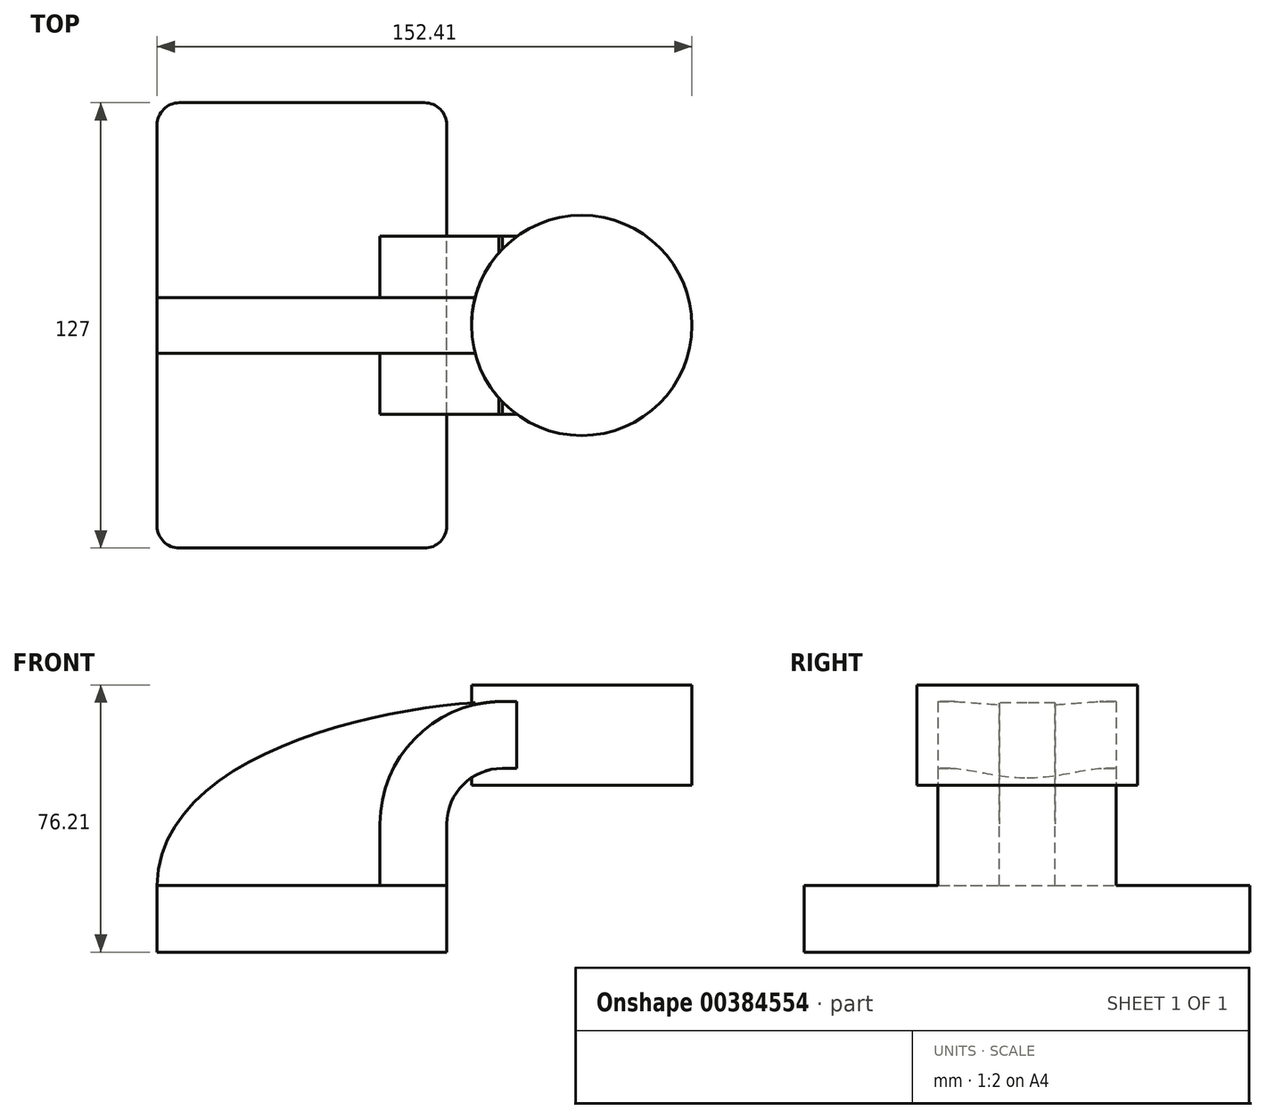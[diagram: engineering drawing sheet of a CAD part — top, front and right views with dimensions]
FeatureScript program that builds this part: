
annotation { "Feature Type Name" : "Feature", "Feature Type Description" : "" }
export const myFeature = defineFeature(function(context is Context, id is Id, definition is map)
    precondition{}
    {
        {
            var Q0;
            Q0=qCreatedBy(makeId("Front.planeOp"),FACE);
            var sketch = newSketch(context, id + "F0", { "sketchPlane" : qUnion([Q0])});
            skLineSegment(sketch, "E0.bottom", {"start": v(-41.28, -9.53) * mm, "end": v(41.28, -9.53) * mm});
            skLineSegment(sketch, "E0.top", {"start": v(-41.28, 9.53) * mm, "end": v(41.28, 9.53) * mm});
            skLineSegment(sketch, "E0.left", {"start": v(-41.28, -9.53) * mm, "end": v(-41.28, 9.53) * mm});
            skLineSegment(sketch, "E0.right", {"start": v(41.27, -9.53) * mm, "end": v(41.27, 9.53) * mm});
            skPoint(sketch, "E0.middle", {"position": v(0, 0) * mm});
            skLineSegment(sketch, "E1.bottom", {"start": v(60.33, 38.1) * mm, "end": v(111.12, 38.1) * mm});
            skLineSegment(sketch, "E1.top", {"start": v(60.33, 66.67) * mm, "end": v(111.12, 66.67) * mm});
            skLineSegment(sketch, "E1.left", {"start": v(60.33, 38.1) * mm, "end": v(60.33, 66.67) * mm});
            skLineSegment(sketch, "E1.right", {"start": v(111.12, 38.1) * mm, "end": v(111.12, 66.67) * mm});
            skPoint(sketch, "E1.middle", {"position": v(85.72, 52.39) * mm});
            skLineSegment(sketch, "E2", {"start": v(41.27, 9.53) * mm, "end": v(41.27, 27) * mm});
            skArc(sketch, "E3", {"start": v(41.28, 27) * mm, "mid": v(45.92, 38.23) * mm, "end": v(57.15, 42.88) * mm});
            skLineSegment(sketch, "E4", {"start": v(57.15, 42.88) * mm, "end": v(79.71, 42.88) * mm});
            skLineSegment(sketch, "E5.0", {"start": v(12.5, -110.82) * mm, "end": v(12.5, -80.96) * mm});
            skLineSegment(sketch, "E6.0", {"start": v(57.15, 61.93) * mm, "end": v(79.71, 61.93) * mm});
            skArc(sketch, "E6.1", {"start": v(22.23, 27) * mm, "mid": v(32.45, 51.7) * mm, "end": v(57.15, 61.93) * mm});
            skLineSegment(sketch, "E6.2", {"start": v(22.23, 9.53) * mm, "end": v(22.23, 27) * mm});
            skLineSegment(sketch, "E7", {"start": v(79.71, 38.1) * mm, "end": v(79.71, 66.67) * mm});
            skFitSpline(sketch, "E8", {"points": [v(-41.28, 9.53) * mm, v(57.15, 61.93) * mm], "startDerivative": vector(1.99, 115.83) * mm, "endDerivative": vector(93.66, 1.04) * mm});
            skSolve(sketch);
        }
        {
            var Q0;
            Q0=makeQuery(id+"F0.imprint","IMPRINT",FACE,{"disambiguationData":[TD([[makeQuery(id+"F0.imprint","IMPRINT",EDGE,{"derivedFrom":sQuery(id+"F0.wireOp",EDGE,"E0.bottom")}),1.0]])]});
            extrude(context, id + "F1", {"entities" : qUnion([Q0]), "endBound" : BoundingType.SYMMETRIC, "depth" : 127 * mm});
        }
        {
            var Q0;
            {var subQ1=sQuery(id+"F0.wireOp",EDGE,"E2");Q0=makeQuery(id+"F0.imprint","IMPRINT",FACE,{"disambiguationData":[TD([[makeQuery(id+"F0.imprint","IMPRINT",EDGE,{"derivedFrom":subQ1}),1.0]])]});}
            var Q1;
            {var subQ0=sQuery(id+"F0.wireOp",EDGE,"E4");var subQ1=sQuery(id+"F0.wireOp",EDGE,"E1.left");var subQ2=makeQuery(id+"F0.imprint","INTERSECT",VERTEX,{"derivedFrom":[subQ1,subQ0]});Q1=makeQuery(id+"F0.imprint","IMPRINT",FACE,{"disambiguationData":[TD([[makeQuery(id+"F0.imprint","IMPRINT",EDGE,{"disambiguationData":[TD([[subQ2,-1.0]])],"derivedFrom":subQ1}),-1.0]])]});}
            extrude(context, id + "F2", {"entities" : qUnion([Q0, Q1]), "operationType" : NewBodyOperationType.ADD, "endBound" : BoundingType.SYMMETRIC, "depth" : 50.8 * mm});
        }
        {
            var Q0;
            {var subQ3=sQuery(id+"F0.wireOp",EDGE,"E6.2");Q0=makeQuery(id+"F0.imprint","IMPRINT",FACE,{"disambiguationData":[TD([[makeQuery(id+"F0.imprint","IMPRINT",EDGE,{"derivedFrom":subQ3}),1.0]])]});}
            extrude(context, id + "F3", {"entities" : qUnion([Q0]), "operationType" : NewBodyOperationType.ADD, "endBound" : BoundingType.SYMMETRIC, "depth" : 15.88 * mm});
        }
        {
            var Q0;
            {var subQ4=sQuery(id+"F0.wireOp",EDGE,"E1.right");Q0=makeQuery(id+"F0.imprint","IMPRINT",FACE,{"disambiguationData":[TD([[makeQuery(id+"F0.imprint","IMPRINT",EDGE,{"derivedFrom":subQ4}),1.0]])]});}
            var Q1;
            Q1=sQuery(id+"F0.wireOp",EDGE,"E7");
            revolve(context, id + "F4", {"operationType" : NewBodyOperationType.ADD, "entities" : qUnion([Q0]), "axis" : qUnion([Q1]), "revolveType" : RevolveType.FULL});
        }
        {
            var Q0;
            Q0=makeQuery(id+"F1.opExtrude","CAP_EDGE",EDGE,{"disambiguationData":[OSD([sQuery(id+"F0.wireOp",EDGE,"E0.right")])],"isStart":true});
            var Q1;
            Q1=makeQuery(id+"F1.opExtrude","CAP_EDGE",EDGE,{"disambiguationData":[OSD([sQuery(id+"F0.wireOp",EDGE,"E0.left")])],"isStart":true});
            var Q2;
            Q2=makeQuery(id+"F1.opExtrude","CAP_EDGE",EDGE,{"disambiguationData":[OSD([sQuery(id+"F0.wireOp",EDGE,"E0.left")])],"isStart":false});
            var Q3;
            Q3=makeQuery(id+"F1.opExtrude","CAP_EDGE",EDGE,{"disambiguationData":[OSD([sQuery(id+"F0.wireOp",EDGE,"E0.right")])],"isStart":false});
            fillet(context, id + "F5", {"entities" : qUnion([Q0, Q1, Q2, Q3]), "radius" : 6.35 * mm, "tangentPropagation" : true, "allowEdgeOverflow" : false});
        }
    });
